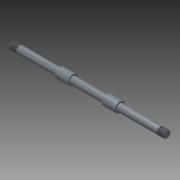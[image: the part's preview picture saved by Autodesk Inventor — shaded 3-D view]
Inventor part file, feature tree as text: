
AUTODESK INVENTOR PART (.ipt)
format: ipt  version: 2015 (Build 190159000, 159)  size: 95,232 bytes
history: native  units: mm
features: thread x2, revolve x1, chamfer x1, sketch x1
ambient origin geometry x8: Origin, YZ Plane, XZ Plane, XY Plane, X Axis, Y Axis, Z Axis, Center Point
bodies: 实体1 (feature_tree)
feature tree (5):
  revolve  "旋转1"  [1 undecoded]
  thread  "螺纹1"  [1 undecoded]
  thread  "螺纹2"  [1 undecoded]
  chamfer  "倒角1"  Distance=9.0mm
  sketch  "草图1"  dims[d0=2.5mm d1=5.0mm d2=28.0mm d3=1.0mm d4=9.0mm d5=24.0mm d6=9.0mm d7=33.0mm d8=90.0deg d9=5.0mm d10=0.0mm d11=5.0mm d12=0.0mm d13=0.25mm d14=2.0mm d15=45.0deg]
note: 3 required parameter values undecoded (feature->parameter linkage not recoverable at this tier; creation-order binding heuristic only, values carry confidence <= 0.55)